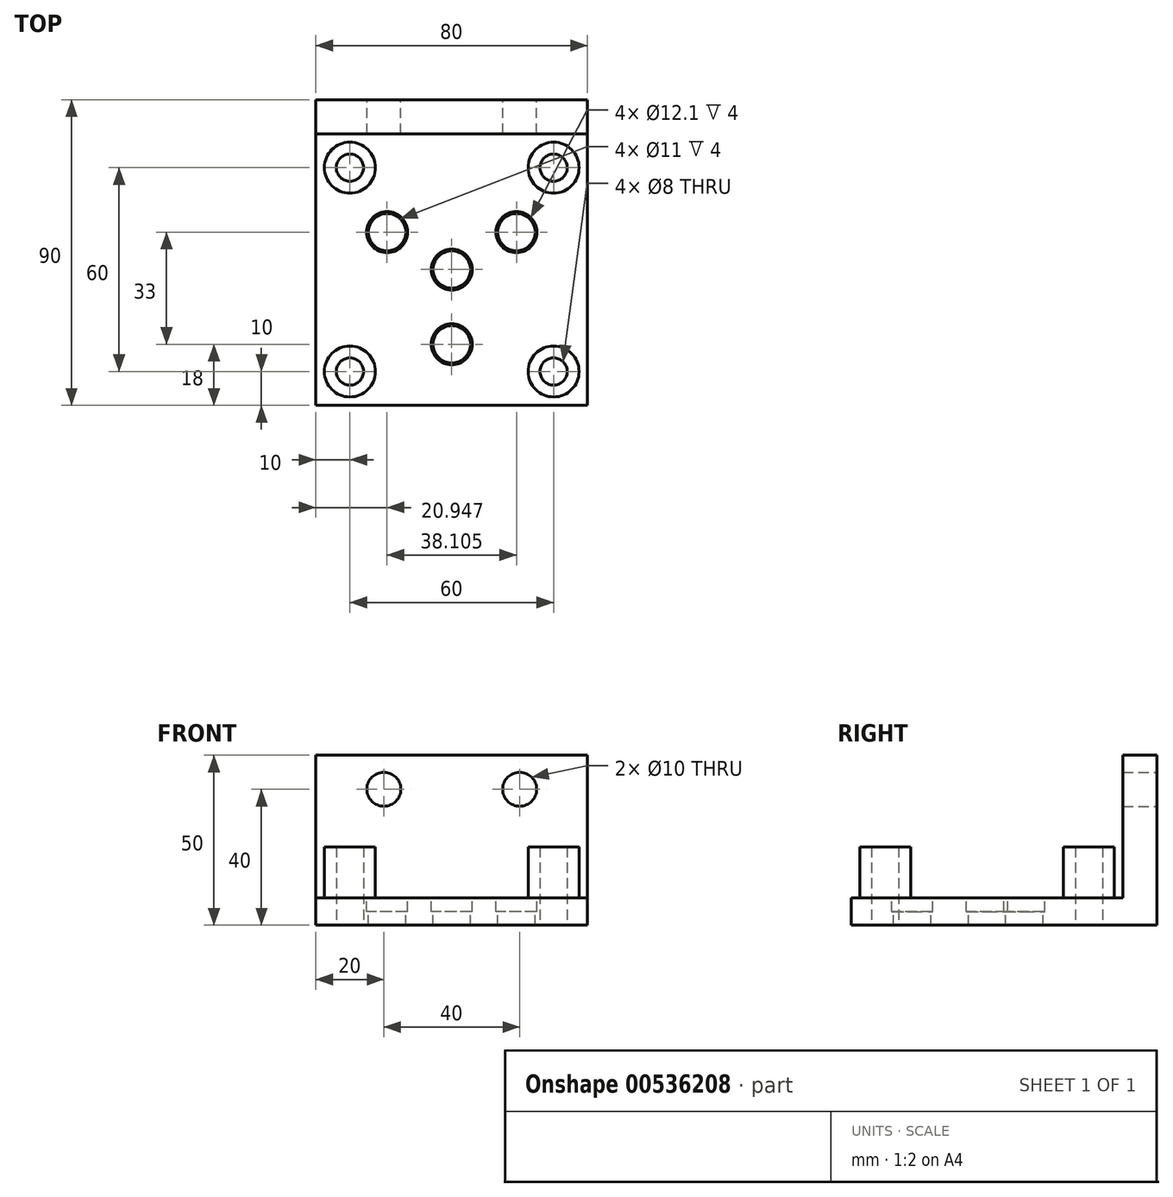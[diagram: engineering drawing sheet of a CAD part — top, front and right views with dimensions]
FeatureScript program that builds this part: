
annotation { "Feature Type Name" : "Feature", "Feature Type Description" : "" }
export const myFeature = defineFeature(function(context is Context, id is Id, definition is map)
    precondition{}
    {
        {
            var Q0;
            Q0=qCreatedBy(makeId("Top.planeOp"),FACE);
            var sketch = newSketch(context, id + "F0", { "sketchPlane" : qUnion([Q0])});
            skLineSegment(sketch, "E0.bottom", {"start": v(40, 40) * mm, "end": v(-40, 40) * mm});
            skLineSegment(sketch, "E0.top", {"start": v(40, -40) * mm, "end": v(-40, -40) * mm});
            skLineSegment(sketch, "E0.left", {"start": v(40, 40) * mm, "end": v(40, -40) * mm});
            skLineSegment(sketch, "E0.right", {"start": v(-40, 40) * mm, "end": v(-40, -40) * mm});
            skPoint(sketch, "E0.middle", {"position": v(0, 0) * mm});
            skSolve(sketch);
        }
        {
            var Q0;
            Q0=makeQuery(id+"F0.imprint","IMPRINT",FACE,{"disambiguationData":[TD([[makeQuery(id+"F0.imprint","IMPRINT",EDGE,{"derivedFrom":sQuery(id+"F0.wireOp",EDGE,"E0.bottom")}),1.0]])]});
            extrude(context, id + "F1", {"entities" : qUnion([Q0]), "depth" : 8 * mm, "offsetDistance" : 25 * mm});
        }
        {
            var Q0;
            Q0=makeQuery(id+"F1.opExtrude","CAP_FACE",FACE,{"disambiguationData":[OSD([sQuery(id+"F0.wireOp",EDGE,"E0.bottom"),sQuery(id+"F0.wireOp",EDGE,"E0.top"),sQuery(id+"F0.wireOp",EDGE,"E0.left"),sQuery(id+"F0.wireOp",EDGE,"E0.right")])],"isStart":false});
            var sketch = newSketch(context, id + "F2", { "sketchPlane" : qUnion([Q0])});
            skCircle(sketch, "E1", {"center": v(0, 0) * mm, "radius": 6.05 * mm});
            skLineSegment(sketch, "E2", {"start": v(0, 0) * mm, "end": v(0, -22) * mm, "construction": true});
            skLineSegment(sketch, "E3.1.0", {"start": v(0, 0) * mm, "end": v(19.05, 11) * mm, "construction": true});
            skLineSegment(sketch, "E3.2.0", {"start": v(0, 0) * mm, "end": v(-19.05, 11) * mm, "construction": true});
            skCircle(sketch, "E4", {"center": v(-19.05, 11) * mm, "radius": 6.05 * mm});
            skCircle(sketch, "E5", {"center": v(19.05, 11) * mm, "radius": 6.05 * mm});
            skCircle(sketch, "E6", {"center": v(0, -22) * mm, "radius": 6.05 * mm});
            skCircle(sketch, "E7", {"center": v(-19.05, 11) * mm, "radius": 5.5 * mm});
            skCircle(sketch, "E8", {"center": v(19.05, 11) * mm, "radius": 5.5 * mm});
            skCircle(sketch, "E9", {"center": v(0, -22) * mm, "radius": 5.5 * mm});
            skCircle(sketch, "E10", {"center": v(0, 0) * mm, "radius": 5.5 * mm});
            skSolve(sketch);
        }
        {
            var Q0;
            Q0=makeQuery(id+"F2.imprint","IMPRINT",FACE,{"disambiguationData":[TD([[makeQuery(id+"F2.imprint","IMPRINT",EDGE,{"derivedFrom":sQuery(id+"F2.wireOp",EDGE,"E4")}),1.0]])]});
            var Q1;
            Q1=makeQuery(id+"F2.imprint","IMPRINT",FACE,{"disambiguationData":[TD([[makeQuery(id+"F2.imprint","IMPRINT",EDGE,{"derivedFrom":sQuery(id+"F2.wireOp",EDGE,"E5")}),1.0]])]});
            var Q2;
            Q2=makeQuery(id+"F2.imprint","IMPRINT",FACE,{"disambiguationData":[TD([[makeQuery(id+"F2.imprint","IMPRINT",EDGE,{"derivedFrom":sQuery(id+"F2.wireOp",EDGE,"E1")}),1.0]])]});
            var Q3;
            Q3=makeQuery(id+"F2.imprint","IMPRINT",FACE,{"disambiguationData":[TD([[makeQuery(id+"F2.imprint","IMPRINT",EDGE,{"derivedFrom":sQuery(id+"F2.wireOp",EDGE,"E6")}),1.0]])]});
            extrude(context, id + "F3", {"entities" : qUnion([Q0, Q1, Q2, Q3]), "operationType" : NewBodyOperationType.REMOVE, "oppositeDirection" : true, "depth" : 4 * mm, "offsetDistance" : 25 * mm});
        }
        {
            var Q0;
            Q0=makeQuery(id+"F3.boolean.opBoolean","SPLIT",FACE,{"disambiguationData":[TD([makeQuery(id+"F3.opExtrude","SWEPT_FACE",FACE,{"disambiguationData":[OSD([sQuery(id+"F2.wireOp",EDGE,"E7")])]})])],"derivedFrom":makeQuery(id+"F1.opExtrude","CAP_FACE",FACE,{"disambiguationData":[OSD([sQuery(id+"F0.wireOp",EDGE,"E0.bottom"),sQuery(id+"F0.wireOp",EDGE,"E0.top"),sQuery(id+"F0.wireOp",EDGE,"E0.left"),sQuery(id+"F0.wireOp",EDGE,"E0.right")])],"isStart":false})});
            var Q1;
            Q1=makeQuery(id+"F3.boolean.opBoolean","SPLIT",FACE,{"disambiguationData":[TD([makeQuery(id+"F3.opExtrude","SWEPT_FACE",FACE,{"disambiguationData":[OSD([sQuery(id+"F2.wireOp",EDGE,"E8")])]})])],"derivedFrom":makeQuery(id+"F1.opExtrude","CAP_FACE",FACE,{"disambiguationData":[OSD([sQuery(id+"F0.wireOp",EDGE,"E0.bottom"),sQuery(id+"F0.wireOp",EDGE,"E0.top"),sQuery(id+"F0.wireOp",EDGE,"E0.left"),sQuery(id+"F0.wireOp",EDGE,"E0.right")])],"isStart":false})});
            var Q2;
            Q2=makeQuery(id+"F3.boolean.opBoolean","SPLIT",FACE,{"disambiguationData":[TD([makeQuery(id+"F3.opExtrude","SWEPT_FACE",FACE,{"disambiguationData":[OSD([sQuery(id+"F2.wireOp",EDGE,"E9")])]})])],"derivedFrom":makeQuery(id+"F1.opExtrude","CAP_FACE",FACE,{"disambiguationData":[OSD([sQuery(id+"F0.wireOp",EDGE,"E0.bottom"),sQuery(id+"F0.wireOp",EDGE,"E0.top"),sQuery(id+"F0.wireOp",EDGE,"E0.left"),sQuery(id+"F0.wireOp",EDGE,"E0.right")])],"isStart":false})});
            extrude(context, id + "F4", {"entities" : qUnion([Q0, Q1, Q2]), "operationType" : NewBodyOperationType.REMOVE, "oppositeDirection" : true, "depth" : 25 * mm, "offsetDistance" : 25 * mm});
        }
        {
            var Q0;
            Q0=makeQuery(id+"F3.boolean.opBoolean","SPLIT",FACE,{"disambiguationData":[TD([makeQuery(id+"F3.opExtrude","SWEPT_FACE",FACE,{"disambiguationData":[OSD([sQuery(id+"F2.wireOp",EDGE,"E10")])]})])],"derivedFrom":makeQuery(id+"F1.opExtrude","CAP_FACE",FACE,{"disambiguationData":[OSD([sQuery(id+"F0.wireOp",EDGE,"E0.bottom"),sQuery(id+"F0.wireOp",EDGE,"E0.top"),sQuery(id+"F0.wireOp",EDGE,"E0.left"),sQuery(id+"F0.wireOp",EDGE,"E0.right")])],"isStart":false})});
            extrude(context, id + "F5", {"entities" : qUnion([Q0]), "operationType" : NewBodyOperationType.REMOVE, "oppositeDirection" : true, "depth" : 25 * mm, "offsetDistance" : 25 * mm});
        }
        {
            var Q0;
            {var subQ0=sQuery(id+"F0.wireOp",EDGE,"E0.left");var subQ1=sQuery(id+"F0.wireOp",EDGE,"E0.top");var subQ2=sQuery(id+"F0.wireOp",EDGE,"E0.right");var subQ3=sQuery(id+"F0.wireOp",EDGE,"E0.bottom");Q0=makeQuery(id+"F3.boolean.opBoolean","SPLIT",FACE,{"disambiguationData":[TD([makeQuery(id+"F1.opExtrude","SWEPT_FACE",FACE,{"disambiguationData":[OSD([subQ3])]})])],"derivedFrom":makeQuery(id+"F1.opExtrude","CAP_FACE",FACE,{"disambiguationData":[OSD([subQ3,subQ1,subQ0,subQ2])],"isStart":false})});}
            var sketch = newSketch(context, id + "F6", { "sketchPlane" : qUnion([Q0])});
            skLineSegment(sketch, "E11", {"start": v(-40, 40) * mm, "end": v(-30, 40) * mm, "construction": true});
            skLineSegment(sketch, "E12", {"start": v(-30, 40) * mm, "end": v(-30, 30) * mm, "construction": true});
            skCircle(sketch, "E13", {"center": v(-30, 30) * mm, "radius": 7.5 * mm});
            skCircle(sketch, "E14.0.1.0", {"center": v(-30, -30) * mm, "radius": 7.5 * mm});
            skCircle(sketch, "E14.1.0.0", {"center": v(30, 30) * mm, "radius": 7.5 * mm});
            skCircle(sketch, "E14.1.1.0", {"center": v(30, -30) * mm, "radius": 7.5 * mm});
            skLineSegment(sketch, "E14.direction1", {"start": v(-30, 30) * mm, "end": v(30, 30) * mm, "construction": true});
            skLineSegment(sketch, "E14.direction2", {"start": v(-30, 30) * mm, "end": v(-30, -30) * mm, "construction": true});
            skCircle(sketch, "E15", {"center": v(-30, 30) * mm, "radius": 4 * mm});
            skCircle(sketch, "E16.0.1.0", {"center": v(-30, -30) * mm, "radius": 4 * mm});
            skCircle(sketch, "E16.1.0.0", {"center": v(30, 30) * mm, "radius": 4 * mm});
            skCircle(sketch, "E16.1.1.0", {"center": v(30, -30) * mm, "radius": 4 * mm});
            skSolve(sketch);
        }
        {
            var Q0;
            Q0=makeQuery(id+"F6.imprint","IMPRINT",FACE,{"disambiguationData":[TD([[makeQuery(id+"F6.imprint","IMPRINT",EDGE,{"derivedFrom":sQuery(id+"F6.wireOp",EDGE,"E13")}),1.0]])]});
            var Q1;
            Q1=makeQuery(id+"F6.imprint","IMPRINT",FACE,{"disambiguationData":[TD([[makeQuery(id+"F6.imprint","IMPRINT",EDGE,{"derivedFrom":sQuery(id+"F6.wireOp",EDGE,"E14.1.0.0")}),1.0]])]});
            var Q2;
            Q2=makeQuery(id+"F6.imprint","IMPRINT",FACE,{"disambiguationData":[TD([[makeQuery(id+"F6.imprint","IMPRINT",EDGE,{"derivedFrom":sQuery(id+"F6.wireOp",EDGE,"E14.1.1.0")}),1.0]])]});
            var Q3;
            Q3=makeQuery(id+"F6.imprint","IMPRINT",FACE,{"disambiguationData":[TD([[makeQuery(id+"F6.imprint","IMPRINT",EDGE,{"derivedFrom":sQuery(id+"F6.wireOp",EDGE,"E14.0.1.0")}),1.0]])]});
            var Q4;
            Q4=sQuery(id+"F6.wireOp",EDGE,"E13");
            extrude(context, id + "F7", {"entities" : qUnion([Q0, Q1, Q2, Q3]), "operationType" : NewBodyOperationType.ADD, "surfaceEntities" : qUnion([Q4]), "depth" : 13 * mm, "offsetDistance" : 25 * mm});
        }
        {
            var Q0;
            {var subQ0=sQuery(id+"F0.wireOp",EDGE,"E0.left");var subQ1=sQuery(id+"F0.wireOp",EDGE,"E0.top");var subQ2=sQuery(id+"F0.wireOp",EDGE,"E0.right");var subQ3=sQuery(id+"F0.wireOp",EDGE,"E0.bottom");Q0=makeQuery(id+"F7.boolean.opBoolean","SPLIT",FACE,{"disambiguationData":[TD([makeQuery(id+"F7.opExtrude","SWEPT_FACE",FACE,{"disambiguationData":[OSD([sQuery(id+"F6.wireOp",EDGE,"E15")])]})])],"derivedFrom":makeQuery(id+"F3.boolean.opBoolean","SPLIT",FACE,{"disambiguationData":[TD([makeQuery(id+"F1.opExtrude","SWEPT_FACE",FACE,{"disambiguationData":[OSD([subQ3])]})])],"derivedFrom":makeQuery(id+"F1.opExtrude","CAP_FACE",FACE,{"disambiguationData":[OSD([subQ3,subQ1,subQ0,subQ2])],"isStart":false})})});}
            var Q1;
            {var subQ0=sQuery(id+"F0.wireOp",EDGE,"E0.left");var subQ1=sQuery(id+"F0.wireOp",EDGE,"E0.top");var subQ2=sQuery(id+"F0.wireOp",EDGE,"E0.right");var subQ3=sQuery(id+"F0.wireOp",EDGE,"E0.bottom");Q1=makeQuery(id+"F7.boolean.opBoolean","SPLIT",FACE,{"disambiguationData":[TD([makeQuery(id+"F7.opExtrude","SWEPT_FACE",FACE,{"disambiguationData":[OSD([sQuery(id+"F6.wireOp",EDGE,"E16.1.0.0")])]})])],"derivedFrom":makeQuery(id+"F3.boolean.opBoolean","SPLIT",FACE,{"disambiguationData":[TD([makeQuery(id+"F1.opExtrude","SWEPT_FACE",FACE,{"disambiguationData":[OSD([subQ3])]})])],"derivedFrom":makeQuery(id+"F1.opExtrude","CAP_FACE",FACE,{"disambiguationData":[OSD([subQ3,subQ1,subQ0,subQ2])],"isStart":false})})});}
            var Q2;
            {var subQ0=sQuery(id+"F0.wireOp",EDGE,"E0.left");var subQ1=sQuery(id+"F0.wireOp",EDGE,"E0.top");var subQ2=sQuery(id+"F0.wireOp",EDGE,"E0.right");var subQ3=sQuery(id+"F0.wireOp",EDGE,"E0.bottom");Q2=makeQuery(id+"F7.boolean.opBoolean","SPLIT",FACE,{"disambiguationData":[TD([makeQuery(id+"F7.opExtrude","SWEPT_FACE",FACE,{"disambiguationData":[OSD([sQuery(id+"F6.wireOp",EDGE,"E16.0.1.0")])]})])],"derivedFrom":makeQuery(id+"F3.boolean.opBoolean","SPLIT",FACE,{"disambiguationData":[TD([makeQuery(id+"F1.opExtrude","SWEPT_FACE",FACE,{"disambiguationData":[OSD([subQ3])]})])],"derivedFrom":makeQuery(id+"F1.opExtrude","CAP_FACE",FACE,{"disambiguationData":[OSD([subQ3,subQ1,subQ0,subQ2])],"isStart":false})})});}
            var Q3;
            {var subQ0=sQuery(id+"F0.wireOp",EDGE,"E0.left");var subQ1=sQuery(id+"F0.wireOp",EDGE,"E0.top");var subQ2=sQuery(id+"F0.wireOp",EDGE,"E0.right");var subQ3=sQuery(id+"F0.wireOp",EDGE,"E0.bottom");Q3=makeQuery(id+"F7.boolean.opBoolean","SPLIT",FACE,{"disambiguationData":[TD([makeQuery(id+"F7.opExtrude","SWEPT_FACE",FACE,{"disambiguationData":[OSD([sQuery(id+"F6.wireOp",EDGE,"E16.1.1.0")])]})])],"derivedFrom":makeQuery(id+"F3.boolean.opBoolean","SPLIT",FACE,{"disambiguationData":[TD([makeQuery(id+"F1.opExtrude","SWEPT_FACE",FACE,{"disambiguationData":[OSD([subQ3])]})])],"derivedFrom":makeQuery(id+"F1.opExtrude","CAP_FACE",FACE,{"disambiguationData":[OSD([subQ3,subQ1,subQ0,subQ2])],"isStart":false})})});}
            extrude(context, id + "F8", {"entities" : qUnion([Q0, Q1, Q2, Q3]), "operationType" : NewBodyOperationType.REMOVE, "oppositeDirection" : true, "depth" : 25 * mm, "offsetDistance" : 25 * mm});
        }
        {
            var Q0;
            Q0=makeQuery(id+"F1.opExtrude","CAP_FACE",FACE,{"disambiguationData":[OSD([sQuery(id+"F0.wireOp",EDGE,"E0.bottom"),sQuery(id+"F0.wireOp",EDGE,"E0.top"),sQuery(id+"F0.wireOp",EDGE,"E0.left"),sQuery(id+"F0.wireOp",EDGE,"E0.right")])],"isStart":true});
            var sketch = newSketch(context, id + "F9", { "sketchPlane" : qUnion([Q0])});
            skLineSegment(sketch, "E17.bottom", {"start": v(-40, -40) * mm, "end": v(40, -40) * mm});
            skLineSegment(sketch, "E17.top", {"start": v(-40, -50) * mm, "end": v(40, -50) * mm});
            skLineSegment(sketch, "E17.left", {"start": v(-40, -40) * mm, "end": v(-40, -50) * mm});
            skLineSegment(sketch, "E17.right", {"start": v(40, -40) * mm, "end": v(40, -50) * mm});
            skSolve(sketch);
        }
        {
            var Q0;
            Q0 = qSketchRegion(id + "F9", true);
            extrude(context, id + "F10", {"entities" : qUnion([Q0]), "operationType" : NewBodyOperationType.ADD, "oppositeDirection" : true, "depth" : 50 * mm, "offsetDistance" : 25 * mm});
        }
        {
            var Q0;
            Q0=makeQuery(id+"F10.opExtrude","SWEPT_FACE",FACE,{"disambiguationData":[OSD([sQuery(id+"F9.wireOp",EDGE,"E17.top")])]});
            var sketch = newSketch(context, id + "F11", { "sketchPlane" : qUnion([Q0])});
            skLineSegment(sketch, "E18.bottom", {"start": v(0, 50) * mm, "end": v(20, 50) * mm, "construction": true});
            skLineSegment(sketch, "E18.top", {"start": v(0, 40) * mm, "end": v(20, 40) * mm, "construction": true});
            skLineSegment(sketch, "E18.left", {"start": v(0, 50) * mm, "end": v(0, 40) * mm, "construction": true});
            skLineSegment(sketch, "E18.right", {"start": v(20, 50) * mm, "end": v(20, 40) * mm, "construction": true});
            skLineSegment(sketch, "E19.bottom", {"start": v(0, 50) * mm, "end": v(-20, 50) * mm, "construction": true});
            skLineSegment(sketch, "E19.top", {"start": v(0, 40) * mm, "end": v(-20, 40) * mm, "construction": true});
            skLineSegment(sketch, "E19.right", {"start": v(-20, 50) * mm, "end": v(-20, 40) * mm, "construction": true});
            skCircle(sketch, "E20", {"center": v(-20, 40) * mm, "radius": 5 * mm});
            skCircle(sketch, "E21", {"center": v(20, 40) * mm, "radius": 5 * mm});
            skSolve(sketch);
        }
        {
            var Q0;
            Q0 = qSketchRegion(id + "F11", true);
            extrude(context, id + "F12", {"entities" : qUnion([Q0]), "operationType" : NewBodyOperationType.REMOVE, "oppositeDirection" : true, "depth" : 25 * mm, "offsetDistance" : 25 * mm});
        }
        {
            var Q0;
            Q0=makeQuery(id+"F7.opExtrude","CAP_FACE",FACE,{"disambiguationData":[OSD([sQuery(id+"F6.wireOp",EDGE,"E13"),sQuery(id+"F6.wireOp",EDGE,"E15")])],"isStart":false});
            var Q1;
            Q1=makeQuery(id+"F7.opExtrude","CAP_FACE",FACE,{"disambiguationData":[OSD([sQuery(id+"F6.wireOp",EDGE,"E14.0.1.0"),sQuery(id+"F6.wireOp",EDGE,"E16.0.1.0")])],"isStart":false});
            var Q2;
            Q2=makeQuery(id+"F7.opExtrude","CAP_FACE",FACE,{"disambiguationData":[OSD([sQuery(id+"F6.wireOp",EDGE,"E14.1.1.0"),sQuery(id+"F6.wireOp",EDGE,"E16.1.1.0")])],"isStart":false});
            var Q3;
            Q3=makeQuery(id+"F7.opExtrude","CAP_FACE",FACE,{"disambiguationData":[OSD([sQuery(id+"F6.wireOp",EDGE,"E14.1.0.0"),sQuery(id+"F6.wireOp",EDGE,"E16.1.0.0")])],"isStart":false});
            extrude(context, id + "F13", {"entities" : qUnion([Q0, Q1, Q2, Q3]), "operationType" : NewBodyOperationType.ADD, "depth" : 2 * mm, "offsetDistance" : 25 * mm});
        }
    });
